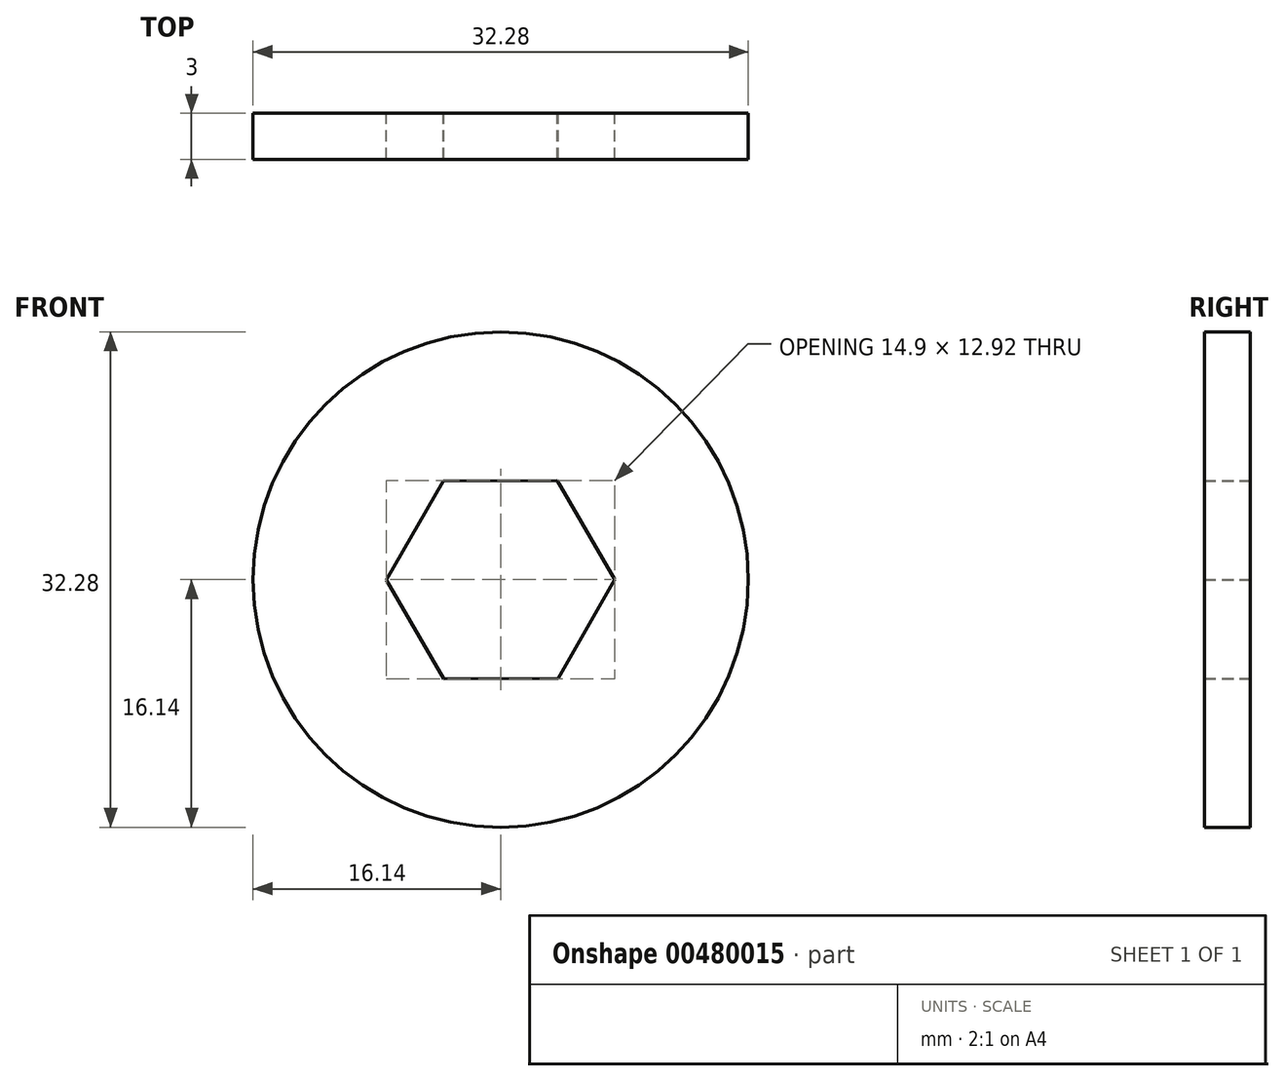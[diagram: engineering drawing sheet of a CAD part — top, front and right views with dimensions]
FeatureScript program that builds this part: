
annotation { "Feature Type Name" : "Feature", "Feature Type Description" : "" }
export const myFeature = defineFeature(function(context is Context, id is Id, definition is map)
    precondition{}
    {
        {
            var Q0;
            Q0=qCreatedBy(makeId("Front.planeOp"),FACE);
            var sketch = newSketch(context, id + "F0", { "sketchPlane" : qUnion([Q0])});
            skCircle(sketch, "E0.cCircle", {"center": v(0, 0) * mm, "radius": 6.45 * mm, "construction": true});
            skLineSegment(sketch, "E0.0", {"start": v(7.45, 0.02) * mm, "end": v(3.74, -6.44) * mm});
            skLineSegment(sketch, "E0.1", {"start": v(3.74, -6.44) * mm, "end": v(-3.7, -6.46) * mm});
            skLineSegment(sketch, "E0.2", {"start": v(-3.7, -6.46) * mm, "end": v(-7.45, -0.02) * mm});
            skLineSegment(sketch, "E0.3", {"start": v(-7.45, -0.02) * mm, "end": v(-3.74, 6.44) * mm});
            skLineSegment(sketch, "E0.4", {"start": v(-3.74, 6.44) * mm, "end": v(3.7, 6.46) * mm});
            skLineSegment(sketch, "E0.5", {"start": v(3.7, 6.46) * mm, "end": v(7.45, 0.02) * mm});
            skPoint(sketch, "E0.0.midPoint", {"position": v(5.6, -3.2) * mm});
            skSolve(sketch);
        }
        {
            var Q0;
            Q0=qCreatedBy(makeId("Front.planeOp"),FACE);
            var sketch = newSketch(context, id + "F1", { "sketchPlane" : qUnion([Q0])});
            skCircle(sketch, "E1", {"center": v(0, 0) * mm, "radius": 16.14 * mm});
            skSolve(sketch);
        }
        {
            var Q0;
            Q0=makeQuery(id+"F1.imprint","IMPRINT",FACE,{"disambiguationData":[TD([[makeQuery(id+"F1.imprint","IMPRINT",EDGE,{"derivedFrom":sQuery(id+"F1.wireOp",EDGE,"E1")}),1.0]])]});
            var Q1;
            Q1=sQuery(id+"F1.wireOp",EDGE,"E1");
            extrude(context, id + "F2", {"entities" : qUnion([Q0]), "surfaceEntities" : qUnion([Q1]), "depth" : 3 * mm});
        }
        {
            var Q0;
            Q0 = qSketchRegion(id + "F0", true);
            extrude(context, id + "F3", {"entities" : qUnion([Q0]), "operationType" : NewBodyOperationType.REMOVE, "depth" : 25 * mm});
        }
    });
